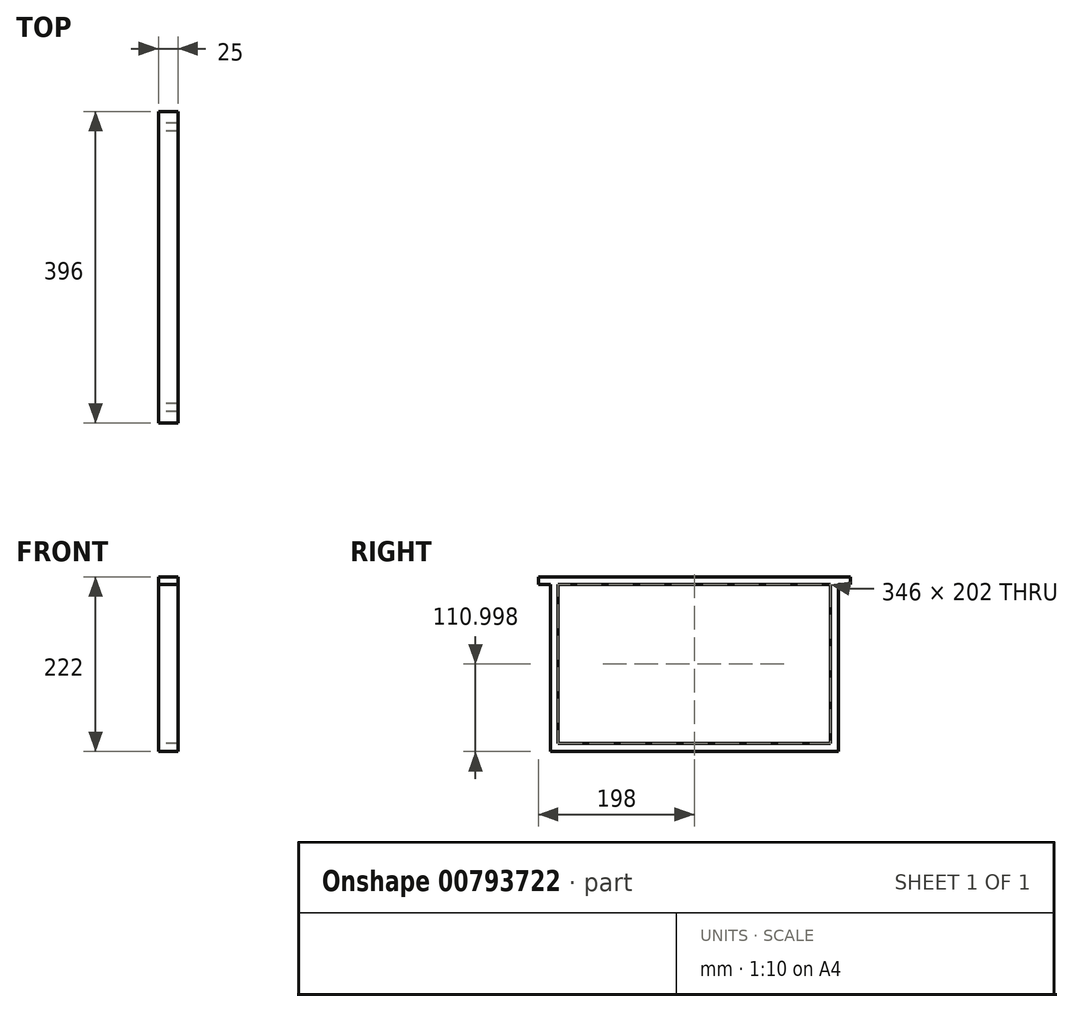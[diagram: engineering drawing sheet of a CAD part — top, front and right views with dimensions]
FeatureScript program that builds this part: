
annotation { "Feature Type Name" : "Feature", "Feature Type Description" : "" }
export const myFeature = defineFeature(function(context is Context, id is Id, definition is map)
    precondition{}
    {
        {
            var Q0;
            Q0=qCreatedBy(makeId("Right.planeOp"),FACE);
            var sketch = newSketch(context, id + "F0", { "sketchPlane" : qUnion([Q0])});
            skLineSegment(sketch, "E0.bottom", {"start": v(198, 151.4) * mm, "end": v(-198, 151.4) * mm});
            skLineSegment(sketch, "E0.top", {"start": v(198, 161.4) * mm, "end": v(-198, 161.4) * mm});
            skLineSegment(sketch, "E0.left", {"start": v(198, 151.4) * mm, "end": v(198, 161.4) * mm});
            skLineSegment(sketch, "E0.right", {"start": v(-198, 151.4) * mm, "end": v(-198, 161.4) * mm});
            skPoint(sketch, "E0.middle", {"position": v(0, 156.4) * mm});
            skLineSegment(sketch, "E1.bottom", {"start": v(183, -60.6) * mm, "end": v(-183, -60.6) * mm});
            skLineSegment(sketch, "E1.top", {"start": v(183, -50.6) * mm, "end": v(-183, -50.6) * mm});
            skLineSegment(sketch, "E1.left", {"start": v(183, -60.6) * mm, "end": v(183, -50.6) * mm});
            skLineSegment(sketch, "E1.right", {"start": v(-183, -60.6) * mm, "end": v(-183, -50.6) * mm});
            skPoint(sketch, "E1.middle", {"position": v(0, -55.6) * mm});
            skLineSegment(sketch, "E2.bottom", {"start": v(-183, -50.6) * mm, "end": v(-173, -50.6) * mm});
            skLineSegment(sketch, "E2.top", {"start": v(-183, 151.4) * mm, "end": v(-173, 151.4) * mm});
            skLineSegment(sketch, "E2.left", {"start": v(-183, -50.6) * mm, "end": v(-183, 151.4) * mm});
            skLineSegment(sketch, "E2.right", {"start": v(-173, -50.6) * mm, "end": v(-173, 151.4) * mm});
            skLineSegment(sketch, "E3.bottom", {"start": v(183, -50.6) * mm, "end": v(173, -50.6) * mm});
            skLineSegment(sketch, "E3.top", {"start": v(183, 151.4) * mm, "end": v(173, 151.4) * mm});
            skLineSegment(sketch, "E3.left", {"start": v(183, -50.6) * mm, "end": v(183, 151.4) * mm});
            skLineSegment(sketch, "E3.right", {"start": v(173, -50.6) * mm, "end": v(173, 151.4) * mm});
            skSolve(sketch);
        }
        {
            var Q0;
            Q0=makeQuery(id+"F0.imprint","IMPRINT",FACE,{"disambiguationData":[TD([[makeQuery(id+"F0.imprint","IMPRINT",EDGE,{"derivedFrom":sQuery(id+"F0.wireOp",EDGE,"E0.top")}),1.0]])]});
            var Q1;
            {var subQ0=sQuery(id+"F0.wireOp",EDGE,"E2.left");Q1=makeQuery(id+"F0.imprint","IMPRINT",FACE,{"disambiguationData":[TD([[makeQuery(id+"F0.imprint","IMPRINT",EDGE,{"derivedFrom":subQ0}),-1.0]])]});}
            var Q2;
            Q2=makeQuery(id+"F0.imprint","IMPRINT",FACE,{"disambiguationData":[TD([[makeQuery(id+"F0.imprint","IMPRINT",EDGE,{"derivedFrom":sQuery(id+"F0.wireOp",EDGE,"E1.bottom")}),-1.0]])]});
            var Q3;
            {var subQ2=sQuery(id+"F0.wireOp",EDGE,"E3.left");Q3=makeQuery(id+"F0.imprint","IMPRINT",FACE,{"disambiguationData":[TD([[makeQuery(id+"F0.imprint","IMPRINT",EDGE,{"derivedFrom":subQ2}),1.0]])]});}
            extrude(context, id + "F1", {"entities" : qUnion([Q0, Q1, Q2, Q3]), "depth" : 25 * mm, "offsetDistance" : 25 * mm});
        }
    });
